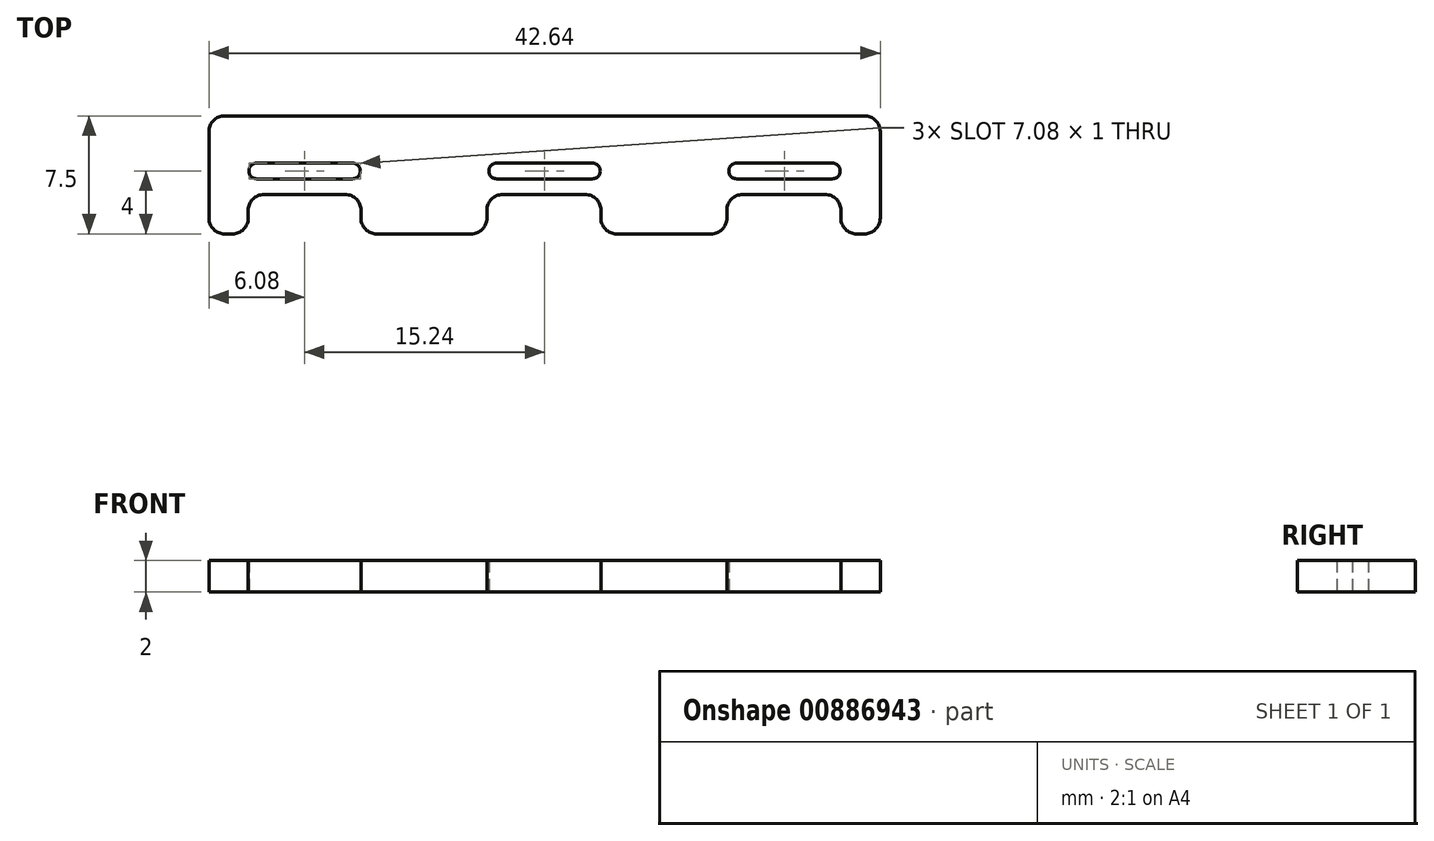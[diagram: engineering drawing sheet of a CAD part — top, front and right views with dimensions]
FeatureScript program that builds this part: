
annotation { "Feature Type Name" : "Feature", "Feature Type Description" : "" }
export const myFeature = defineFeature(function(context is Context, id is Id, definition is map)
    precondition{}
    {
        {
            var Q0;
            Q0=qCreatedBy(makeId("Top.planeOp"),FACE);
            var sketch = newSketch(context, id + "F0", { "sketchPlane" : qUnion([Q0])});
            skLineSegment(sketch, "E0.bottom", {"start": v(0, 0) * mm, "end": v(42.64, 0) * mm});
            skLineSegment(sketch, "E0.top", {"start": v(0, -5) * mm, "end": v(42.64, -5) * mm});
            skLineSegment(sketch, "E0.left", {"start": v(0, 0) * mm, "end": v(0, -5) * mm});
            skLineSegment(sketch, "E0.right", {"start": v(42.64, 0) * mm, "end": v(42.64, -5) * mm});
            skLineSegment(sketch, "E1.bottom", {"start": v(0, -5) * mm, "end": v(2.5, -5) * mm});
            skLineSegment(sketch, "E1.top", {"start": v(0, -7.5) * mm, "end": v(2.5, -7.5) * mm});
            skLineSegment(sketch, "E1.left", {"start": v(0, -5) * mm, "end": v(0, -7.5) * mm});
            skLineSegment(sketch, "E1.right", {"start": v(2.5, -5) * mm, "end": v(2.5, -7.5) * mm});
            skLineSegment(sketch, "E2.bottom", {"start": v(42.64, -5) * mm, "end": v(40.14, -5) * mm});
            skLineSegment(sketch, "E2.top", {"start": v(42.64, -7.5) * mm, "end": v(40.14, -7.5) * mm});
            skLineSegment(sketch, "E2.left", {"start": v(42.64, -5) * mm, "end": v(42.64, -7.5) * mm});
            skLineSegment(sketch, "E2.right", {"start": v(40.14, -5) * mm, "end": v(40.14, -7.5) * mm});
            skLineSegment(sketch, "E3.bottom", {"start": v(9.66, -5) * mm, "end": v(17.66, -5) * mm});
            skLineSegment(sketch, "E3.top", {"start": v(9.66, -7.5) * mm, "end": v(17.66, -7.5) * mm});
            skLineSegment(sketch, "E3.left", {"start": v(9.66, -5) * mm, "end": v(9.66, -7.5) * mm});
            skLineSegment(sketch, "E3.right", {"start": v(17.66, -5) * mm, "end": v(17.66, -7.5) * mm});
            skLineSegment(sketch, "E4.bottom", {"start": v(24.9, -5) * mm, "end": v(32.9, -5) * mm});
            skLineSegment(sketch, "E4.top", {"start": v(24.9, -7.5) * mm, "end": v(32.9, -7.5) * mm});
            skLineSegment(sketch, "E4.left", {"start": v(24.9, -5) * mm, "end": v(24.9, -7.5) * mm});
            skLineSegment(sketch, "E4.right", {"start": v(32.9, -5) * mm, "end": v(32.9, -7.5) * mm});
            skLineSegment(sketch, "E5", {"start": v(3.04, -3.5) * mm, "end": v(9.12, -3.5) * mm});
            skArc(sketch, "E6.0.startCap", {"start": v(3.04, -4) * mm, "mid": v(2.54, -3.5) * mm, "end": v(3.04, -3) * mm});
            skArc(sketch, "E6.0.endCap", {"start": v(9.12, -3) * mm, "mid": v(9.62, -3.5) * mm, "end": v(9.12, -4) * mm});
            skLineSegment(sketch, "E6.0.left", {"start": v(3.04, -3) * mm, "end": v(9.12, -3) * mm});
            skLineSegment(sketch, "E6.0.right", {"start": v(3.04, -4) * mm, "end": v(9.12, -4) * mm});
            skArc(sketch, "E7.1.0.0", {"start": v(18.28, -4) * mm, "mid": v(17.78, -3.5) * mm, "end": v(18.28, -3) * mm});
            skLineSegment(sketch, "E7.1.0.1", {"start": v(18.28, -3) * mm, "end": v(24.36, -3) * mm});
            skArc(sketch, "E7.1.0.2", {"start": v(24.36, -3) * mm, "mid": v(24.86, -3.5) * mm, "end": v(24.36, -4) * mm});
            skLineSegment(sketch, "E7.1.0.3", {"start": v(18.28, -4) * mm, "end": v(24.36, -4) * mm});
            skArc(sketch, "E7.2.0.0", {"start": v(33.52, -4) * mm, "mid": v(33.02, -3.5) * mm, "end": v(33.52, -3) * mm});
            skLineSegment(sketch, "E7.2.0.1", {"start": v(33.52, -3) * mm, "end": v(39.6, -3) * mm});
            skArc(sketch, "E7.2.0.2", {"start": v(39.6, -3) * mm, "mid": v(40.1, -3.5) * mm, "end": v(39.6, -4) * mm});
            skLineSegment(sketch, "E7.2.0.3", {"start": v(33.52, -4) * mm, "end": v(39.6, -4) * mm});
            skLineSegment(sketch, "E7.direction1", {"start": v(3.04, -4) * mm, "end": v(18.28, -4) * mm, "construction": true});
            skLineSegment(sketch, "E8", {"start": v(27.4, -7.5) * mm, "end": v(27.4, 0) * mm});
            skSolve(sketch);
        }
        {
            var Q0;
            {var subQ0=sQuery(id+"F0.wireOp",EDGE,"E4.left");Q0=makeQuery(id+"F0.imprint","IMPRINT",FACE,{"disambiguationData":[TD([[makeQuery(id+"F0.imprint","IMPRINT",EDGE,{"derivedFrom":subQ0}),1.0]])]});}
            var Q1;
            Q1=makeQuery(id+"F0.imprint","IMPRINT",FACE,{"disambiguationData":[TD([[makeQuery(id+"F0.imprint","IMPRINT",EDGE,{"derivedFrom":sQuery(id+"F0.wireOp",EDGE,"E3.top")}),1.0]])]});
            var Q2;
            Q2=makeQuery(id+"F0.imprint","IMPRINT",FACE,{"disambiguationData":[TD([[makeQuery(id+"F0.imprint","IMPRINT",EDGE,{"derivedFrom":sQuery(id+"F0.wireOp",EDGE,"E1.top")}),1.0]])]});
            var Q3;
            {var subQ3=sQuery(id+"F0.wireOp",EDGE,"E0.left");Q3=makeQuery(id+"F0.imprint","IMPRINT",FACE,{"disambiguationData":[TD([[makeQuery(id+"F0.imprint","IMPRINT",EDGE,{"derivedFrom":subQ3}),1.0]])]});}
            var Q4;
            {var subQ0=sQuery(id+"F0.wireOp",EDGE,"E0.right");Q4=makeQuery(id+"F0.imprint","IMPRINT",FACE,{"disambiguationData":[TD([[makeQuery(id+"F0.imprint","IMPRINT",EDGE,{"derivedFrom":subQ0}),-1.0]])]});}
            var Q5;
            {var subQ0=sQuery(id+"F0.wireOp",EDGE,"E4.right");Q5=makeQuery(id+"F0.imprint","IMPRINT",FACE,{"disambiguationData":[TD([[makeQuery(id+"F0.imprint","IMPRINT",EDGE,{"derivedFrom":subQ0}),-1.0]])]});}
            var Q6;
            Q6=makeQuery(id+"F0.imprint","IMPRINT",FACE,{"disambiguationData":[TD([[makeQuery(id+"F0.imprint","IMPRINT",EDGE,{"derivedFrom":sQuery(id+"F0.wireOp",EDGE,"E2.top")}),-1.0]])]});
            extrude(context, id + "F1", {"entities" : qUnion([Q0, Q1, Q2, Q3, Q4, Q5, Q6]), "depth" : 2 * mm, "offsetDistance" : 25 * mm});
        }
        {
            var Q0;
            Q0=makeQuery(id+"F1.opExtrude","SWEPT_EDGE",EDGE,{"disambiguationData":[OSD([sQuery(id+"F0.wireOp",EDGE,"E1.top"),sQuery(id+"F0.wireOp",EDGE,"E1.left")])]});
            var Q1;
            Q1=makeQuery(id+"F1.opExtrude","SWEPT_EDGE",EDGE,{"disambiguationData":[OSD([sQuery(id+"F0.wireOp",EDGE,"E1.top"),sQuery(id+"F0.wireOp",EDGE,"E1.right")])]});
            var Q2;
            Q2=makeQuery(id+"F1.opExtrude","SWEPT_EDGE",EDGE,{"disambiguationData":[OSD([sQuery(id+"F0.wireOp",EDGE,"E0.top"),sQuery(id+"F0.wireOp",EDGE,"E1.right")])]});
            var Q3;
            Q3=makeQuery(id+"F1.opExtrude","SWEPT_EDGE",EDGE,{"disambiguationData":[OSD([sQuery(id+"F0.wireOp",EDGE,"E3.top"),sQuery(id+"F0.wireOp",EDGE,"E3.left")])]});
            var Q4;
            Q4=makeQuery(id+"F1.opExtrude","SWEPT_EDGE",EDGE,{"disambiguationData":[OSD([sQuery(id+"F0.wireOp",EDGE,"E3.top"),sQuery(id+"F0.wireOp",EDGE,"E3.right")])]});
            var Q5;
            Q5=makeQuery(id+"F1.opExtrude","SWEPT_EDGE",EDGE,{"disambiguationData":[OSD([sQuery(id+"F0.wireOp",EDGE,"E0.top"),sQuery(id+"F0.wireOp",EDGE,"E3.right")])]});
            var Q6;
            Q6=makeQuery(id+"F1.opExtrude","SWEPT_EDGE",EDGE,{"disambiguationData":[OSD([sQuery(id+"F0.wireOp",EDGE,"E4.top"),sQuery(id+"F0.wireOp",EDGE,"E4.left")])]});
            var Q7;
            Q7=makeQuery(id+"F1.opExtrude","SWEPT_EDGE",EDGE,{"disambiguationData":[OSD([sQuery(id+"F0.wireOp",EDGE,"E0.top"),sQuery(id+"F0.wireOp",EDGE,"E4.right")])]});
            var Q8;
            Q8=makeQuery(id+"F1.opExtrude","SWEPT_EDGE",EDGE,{"disambiguationData":[OSD([sQuery(id+"F0.wireOp",EDGE,"E4.top"),sQuery(id+"F0.wireOp",EDGE,"E4.right")])]});
            var Q9;
            Q9=makeQuery(id+"F1.opExtrude","SWEPT_EDGE",EDGE,{"disambiguationData":[OSD([sQuery(id+"F0.wireOp",EDGE,"E2.top"),sQuery(id+"F0.wireOp",EDGE,"E2.right")])]});
            var Q10;
            Q10=makeQuery(id+"F1.opExtrude","SWEPT_EDGE",EDGE,{"disambiguationData":[OSD([sQuery(id+"F0.wireOp",EDGE,"E2.top"),sQuery(id+"F0.wireOp",EDGE,"E2.left")])]});
            var Q11;
            Q11=makeQuery(id+"F1.opExtrude","SWEPT_EDGE",EDGE,{"disambiguationData":[OSD([sQuery(id+"F0.wireOp",EDGE,"E0.bottom"),sQuery(id+"F0.wireOp",EDGE,"E0.right")])]});
            var Q12;
            Q12=makeQuery(id+"F1.opExtrude","SWEPT_EDGE",EDGE,{"disambiguationData":[OSD([sQuery(id+"F0.wireOp",EDGE,"E0.top"),sQuery(id+"F0.wireOp",EDGE,"E2.right")])]});
            var Q13;
            Q13=makeQuery(id+"F1.opExtrude","SWEPT_EDGE",EDGE,{"disambiguationData":[OSD([sQuery(id+"F0.wireOp",EDGE,"E0.top"),sQuery(id+"F0.wireOp",EDGE,"E4.left")])]});
            var Q14;
            Q14=makeQuery(id+"F1.opExtrude","SWEPT_EDGE",EDGE,{"disambiguationData":[OSD([sQuery(id+"F0.wireOp",EDGE,"E0.top"),sQuery(id+"F0.wireOp",EDGE,"E3.left")])]});
            var Q15;
            Q15=makeQuery(id+"F1.opExtrude","SWEPT_EDGE",EDGE,{"disambiguationData":[OSD([sQuery(id+"F0.wireOp",EDGE,"E0.bottom"),sQuery(id+"F0.wireOp",EDGE,"E0.left")])]});
            fillet(context, id + "F2", {"entities" : qUnion([Q0, Q1, Q2, Q3, Q4, Q5, Q6, Q7, Q8, Q9, Q10, Q11, Q12, Q13, Q14, Q15]), "radius" : 1 * mm, "tangentPropagation" : true, "allowEdgeOverflow" : false});
        }
    });
